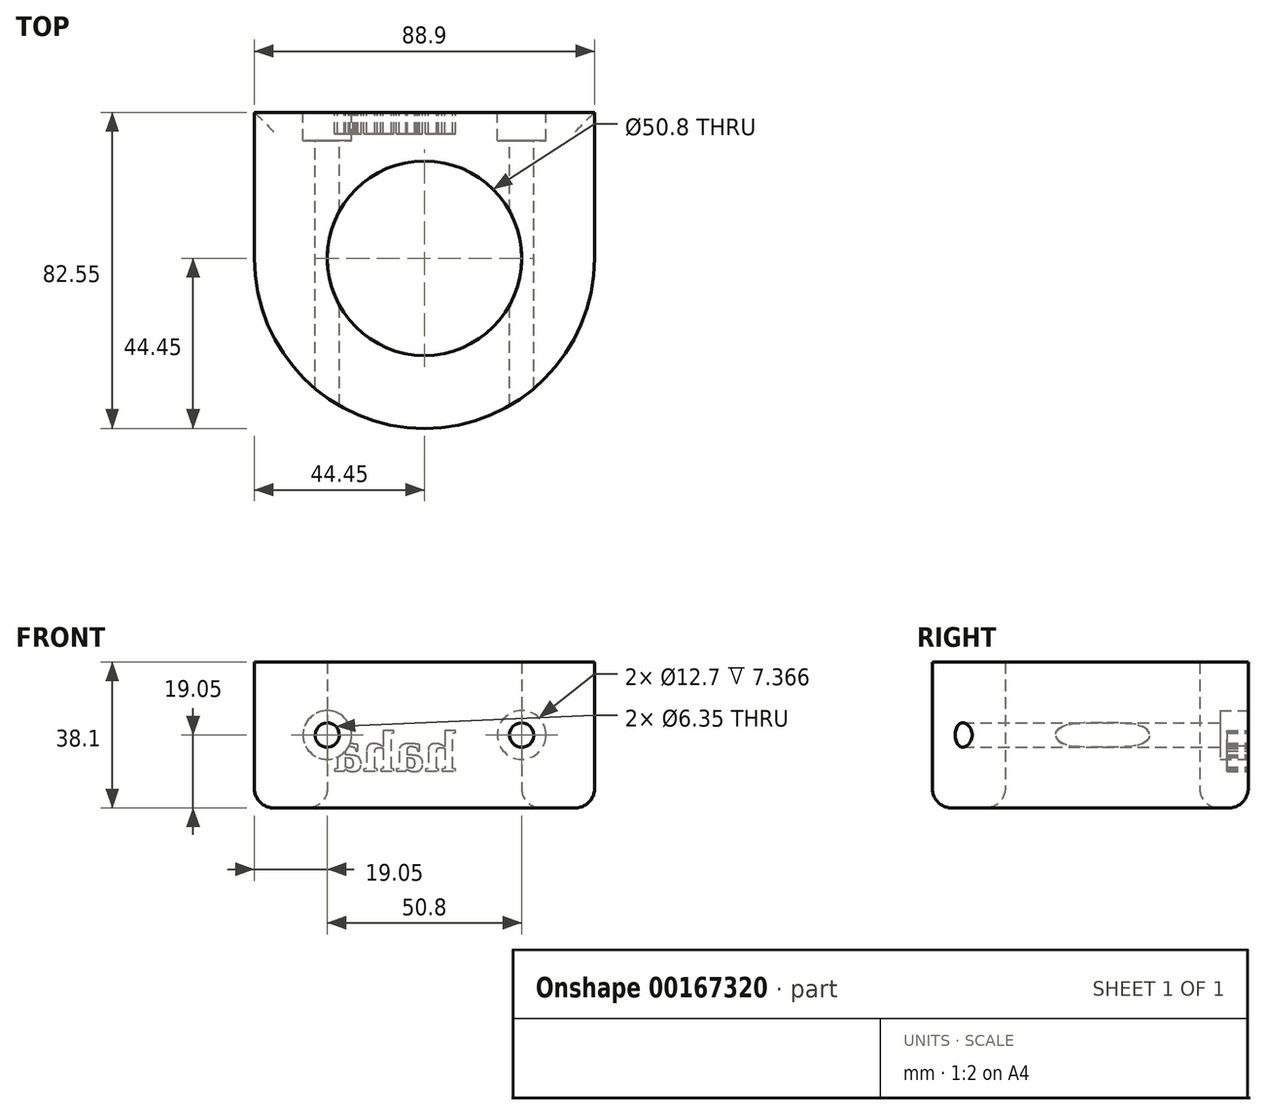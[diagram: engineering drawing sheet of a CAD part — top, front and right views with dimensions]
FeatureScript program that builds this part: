
annotation { "Feature Type Name" : "Feature", "Feature Type Description" : "" }
export const myFeature = defineFeature(function(context is Context, id is Id, definition is map)
    precondition{}
    {
        {
            var Q0;
            Q0=qCreatedBy(makeId("Top.planeOp"),FACE);
            var sketch = newSketch(context, id + "F0", { "sketchPlane" : qUnion([Q0])});
            skCircle(sketch, "E0", {"center": v(0, 0) * mm, "radius": 25.4 * mm});
            skArc(sketch, "E1", {"start": v(-44.45, 0) * mm, "mid": v(0, -44.45) * mm, "end": v(44.45, 0) * mm});
            skLineSegment(sketch, "E2", {"start": v(0, -44.45) * mm, "end": v(0, -44.45) * mm});
            skLineSegment(sketch, "E3", {"start": v(-44.45, 0) * mm, "end": v(-44.45, 38.1) * mm});
            skLineSegment(sketch, "E4", {"start": v(44.45, 0) * mm, "end": v(44.45, 38.1) * mm});
            skLineSegment(sketch, "E5", {"start": v(44.45, 38.1) * mm, "end": v(-44.45, 38.1) * mm});
            skSolve(sketch);
        }
        {
            var Q0;
            Q0 = qSketchRegion(id + "F0", true);
            extrude(context, id + "F1", {"entities" : qUnion([Q0]), "depth" : 38.1 * mm});
        }
        {
            var Q0;
            Q0=makeQuery(id+"F1.opExtrude","SWEPT_FACE",FACE,{"disambiguationData":[OSD([sQuery(id+"F0.wireOp",EDGE,"E5")])]});
            var sketch = newSketch(context, id + "F2", { "sketchPlane" : qUnion([Q0])});
            skCircle(sketch, "E6", {"center": v(-25.4, 19.05) * mm, "radius": 3.18 * mm});
            skCircle(sketch, "E7", {"center": v(25.4, 19.05) * mm, "radius": 3.18 * mm});
            skLineSegment(sketch, "E8", {"start": v(-25.4, 19.05) * mm, "end": v(25.4, 19.05) * mm, "construction": true});
            skLineSegment(sketch, "E9", {"start": v(0, 0) * mm, "end": v(0, 38.1) * mm, "construction": true});
            skSolve(sketch);
        }
        {
            var Q0;
            Q0 = qSketchRegion(id + "F2", true);
            extrude(context, id + "F3", {"entities" : qUnion([Q0]), "operationType" : NewBodyOperationType.REMOVE, "oppositeDirection" : true, "depth" : 96.77 * mm});
        }
        {
            var Q0;
            Q0=makeQuery(id+"F1.opExtrude","SWEPT_FACE",FACE,{"disambiguationData":[OSD([sQuery(id+"F0.wireOp",EDGE,"E5")])]});
            var sketch = newSketch(context, id + "F4", { "sketchPlane" : qUnion([Q0])});
            skCircle(sketch, "E10.0", {"center": v(-25.4, 19.05) * mm, "radius": 3.18 * mm});
            skCircle(sketch, "E11.0", {"center": v(25.4, 19.05) * mm, "radius": 3.18 * mm});
            skCircle(sketch, "E12", {"center": v(-25.4, 19.05) * mm, "radius": 6.35 * mm});
            skCircle(sketch, "E13", {"center": v(25.4, 19.05) * mm, "radius": 6.35 * mm});
            skSolve(sketch);
        }
        {
            var Q0;
            Q0 = qSketchRegion(id + "F4", true);
            extrude(context, id + "F5", {"entities" : qUnion([Q0]), "operationType" : NewBodyOperationType.REMOVE, "oppositeDirection" : true, "depth" : 7.37 * mm});
        }
        {
            var Q0;
            Q0=makeQuery(id+"F1.opExtrude","CAP_FACE",FACE,{"disambiguationData":[OSD([sQuery(id+"F0.wireOp",EDGE,"E0"),sQuery(id+"F0.wireOp",EDGE,"E1"),sQuery(id+"F0.wireOp",EDGE,"E3"),sQuery(id+"F0.wireOp",EDGE,"E4"),sQuery(id+"F0.wireOp",EDGE,"E5")])],"isStart":true});
            fillet(context, id + "F6", {"entities" : qUnion([Q0]), "radius" : 5.08 * mm, "tangentPropagation" : true, "allowEdgeOverflow" : false});
        }
        {
            var Q0;
            Q0=makeQuery(id+"F1.opExtrude","SWEPT_FACE",FACE,{"disambiguationData":[OSD([sQuery(id+"F0.wireOp",EDGE,"E5")])]});
            var sketch = newSketch(context, id + "F7", { "sketchPlane" : qUnion([Q0])});
            skText(sketch, "E14", { "text": "haha", "fontName": "Tinos-Bold.ttf"});
            const initialGuessF7  = {"E14": [-0.00852, 0.00964, 1, 0, 0.01098]};
            skSetInitialGuess(sketch, initialGuessF7);
            skSolve(sketch);
        }
        {
            var Q0;
            Q0 = qSketchRegion(id + "F7", true);
            extrude(context, id + "F8", {"entities" : qUnion([Q0]), "operationType" : NewBodyOperationType.REMOVE, "oppositeDirection" : true, "depth" : 5.6 * mm});
        }
    });
